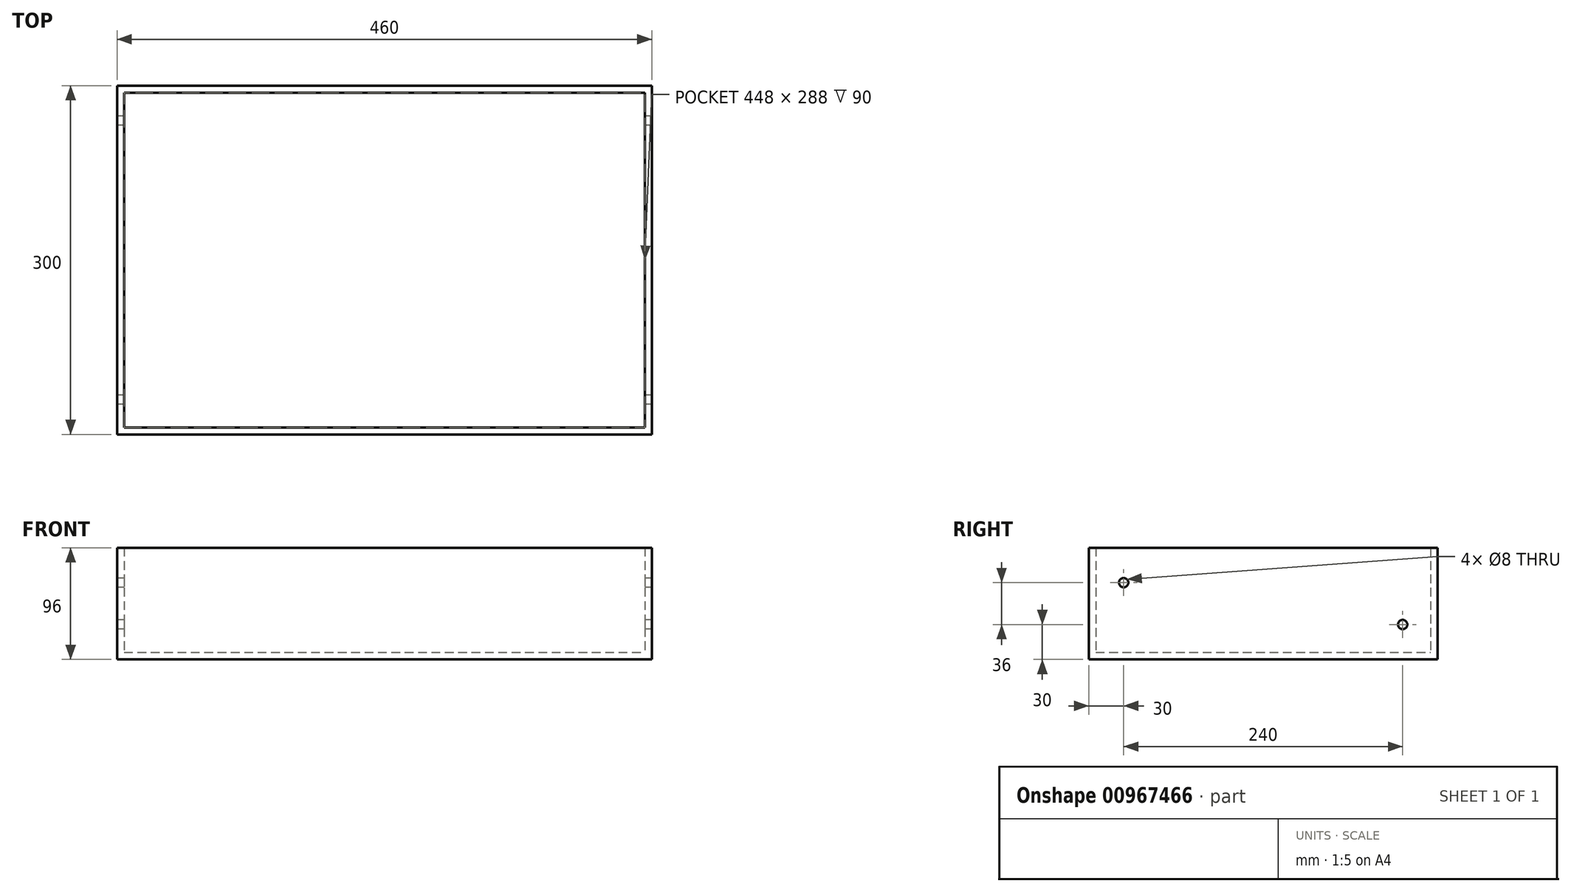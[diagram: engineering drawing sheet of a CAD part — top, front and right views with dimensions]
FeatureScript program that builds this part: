
annotation { "Feature Type Name" : "Feature", "Feature Type Description" : "" }
export const myFeature = defineFeature(function(context is Context, id is Id, definition is map)
    precondition{}
    {
        {
            var Q0;
            Q0=qCreatedBy(makeId("Top.planeOp"),FACE);
            var sketch = newSketch(context, id + "F0", { "sketchPlane" : qUnion([Q0])});
            skLineSegment(sketch, "E0.bottom", {"start": v(230, -150) * mm, "end": v(-230, -150) * mm});
            skLineSegment(sketch, "E0.top", {"start": v(230, 150) * mm, "end": v(-230, 150) * mm});
            skLineSegment(sketch, "E0.left", {"start": v(230, -150) * mm, "end": v(230, 150) * mm});
            skLineSegment(sketch, "E0.right", {"start": v(-230, -150) * mm, "end": v(-230, 150) * mm});
            skPoint(sketch, "E0.middle", {"position": v(0, 0) * mm});
            skSolve(sketch);
        }
        {
            var Q0;
            Q0=makeQuery(id+"F0.imprint","IMPRINT",FACE,{"disambiguationData":[TD([[makeQuery(id+"F0.imprint","IMPRINT",EDGE,{"derivedFrom":sQuery(id+"F0.wireOp",EDGE,"E0.bottom")}),-1.0]])]});
            extrude(context, id + "F1", {"entities" : qUnion([Q0]), "depth" : 6 * mm, "offsetDistance" : 25 * mm});
        }
        {
            var Q0;
            Q0=makeQuery(id+"F1.opExtrude","CAP_FACE",FACE,{"disambiguationData":[OSD([sQuery(id+"F0.wireOp",EDGE,"E0.bottom"),sQuery(id+"F0.wireOp",EDGE,"E0.top"),sQuery(id+"F0.wireOp",EDGE,"E0.left"),sQuery(id+"F0.wireOp",EDGE,"E0.right")])],"isStart":false});
            var sketch = newSketch(context, id + "F2", { "sketchPlane" : qUnion([Q0])});
            skLineSegment(sketch, "E1.bottom", {"start": v(-224, -144) * mm, "end": v(224, -144) * mm});
            skLineSegment(sketch, "E1.top", {"start": v(-224, 144) * mm, "end": v(224, 144) * mm});
            skLineSegment(sketch, "E1.left", {"start": v(-224, -144) * mm, "end": v(-224, 144) * mm});
            skLineSegment(sketch, "E1.right", {"start": v(224, -144) * mm, "end": v(224, 144) * mm});
            skPoint(sketch, "E1.middle", {"position": v(0, 0) * mm});
            skSolve(sketch);
        }
        {
            var Q0;
            Q0=makeQuery(id+"F2.imprint","IMPRINT",FACE,{"disambiguationData":[TD([[makeQuery(id+"F2.imprint","IMPRINT",EDGE,{"derivedFrom":sQuery(id+"F2.wireOp",EDGE,"E1.bottom")}),-1.0]])]});
            extrude(context, id + "F3", {"entities" : qUnion([Q0]), "operationType" : NewBodyOperationType.ADD, "depth" : 90 * mm, "offsetDistance" : 25 * mm});
        }
        {
            var Q0;
            {var subQ0=sQuery(id+"F0.wireOp",EDGE,"E0.right");Q0=makeQuery(id+"F3.boolean.opBoolean","MERGE",FACE,{"derivedFrom":[makeQuery(id+"F1.opExtrude","SWEPT_FACE",FACE,{"disambiguationData":[OSD([subQ0])]}),makeQuery(id+"F3.opExtrude","SWEPT_FACE",FACE,{"disambiguationData":[OSD([subQ0])]})]});}
            var sketch = newSketch(context, id + "F4", { "sketchPlane" : qUnion([Q0])});
            skCircle(sketch, "E2", {"center": v(-120, 30) * mm, "radius": 4 * mm});
            skCircle(sketch, "E3", {"center": v(120, 66) * mm, "radius": 4 * mm});
            skSolve(sketch);
        }
        {
            var Q0;
            Q0=makeQuery(id+"F4.imprint","IMPRINT",FACE,{"disambiguationData":[TD([[makeQuery(id+"F4.imprint","IMPRINT",EDGE,{"derivedFrom":sQuery(id+"F4.wireOp",EDGE,"E2")}),1.0]])]});
            var Q1;
            Q1=makeQuery(id+"F4.imprint","IMPRINT",FACE,{"disambiguationData":[TD([[makeQuery(id+"F4.imprint","IMPRINT",EDGE,{"derivedFrom":sQuery(id+"F4.wireOp",EDGE,"E3")}),1.0]])]});
            var Q2;
            Q2=sQuery(id+"F4.wireOp",EDGE,"E2");
            var Q3;
            Q3=sQuery(id+"F4.wireOp",EDGE,"E3");
            var Q4;
            {var subQ0=sQuery(id+"F0.wireOp",EDGE,"E0.left");Q4=makeQuery(id+"F3.boolean.opBoolean","MERGE",FACE,{"derivedFrom":[makeQuery(id+"F1.opExtrude","SWEPT_FACE",FACE,{"disambiguationData":[OSD([subQ0])]}),makeQuery(id+"F3.opExtrude","SWEPT_FACE",FACE,{"disambiguationData":[OSD([subQ0])]})]});}
            extrude(context, id + "F5", {"entities" : qUnion([Q0, Q1]), "operationType" : NewBodyOperationType.REMOVE, "surfaceEntities" : qUnion([Q2, Q3]), "endBound" : BoundingType.UP_TO_SURFACE, "oppositeDirection" : true, "depth" : 25 * mm, "endBoundEntityFace" : qUnion([Q4]), "offsetDistance" : 25 * mm});
        }
    });
